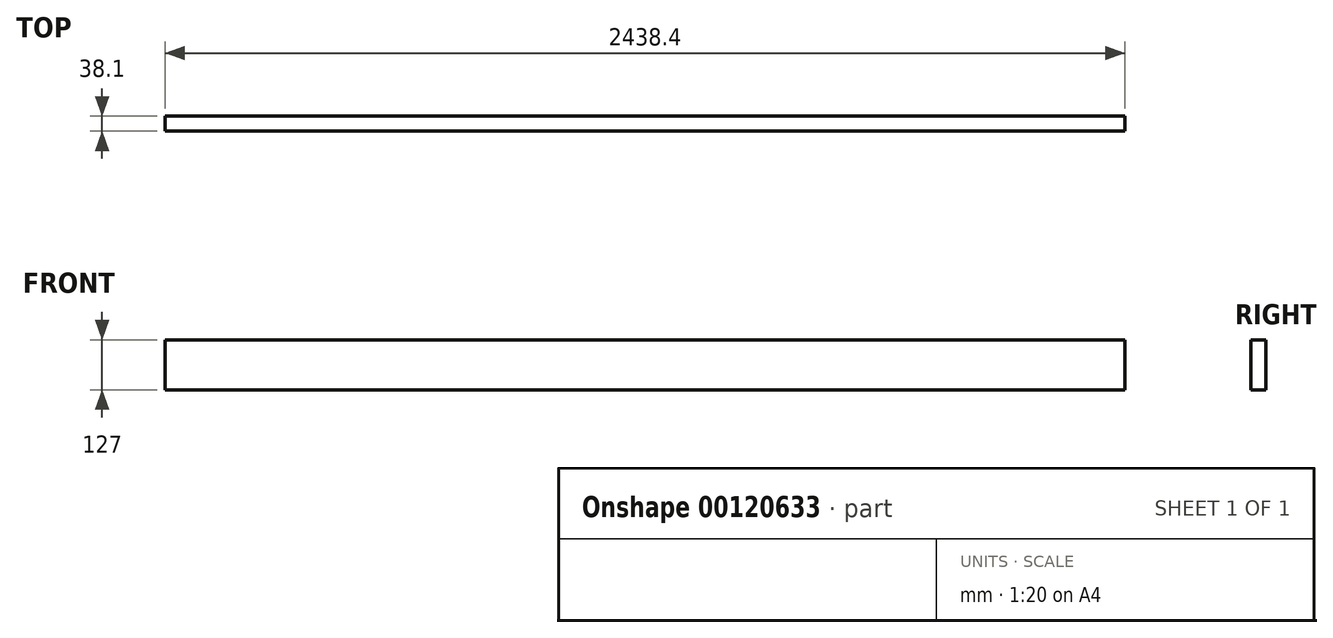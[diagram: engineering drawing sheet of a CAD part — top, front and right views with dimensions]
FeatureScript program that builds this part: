
annotation { "Feature Type Name" : "Feature", "Feature Type Description" : "" }
export const myFeature = defineFeature(function(context is Context, id is Id, definition is map)
    precondition{}
    {
        {
            var Q0;
            Q0=qCreatedBy(makeId("Top.planeOp"),FACE);
            var sketch = newSketch(context, id + "F0", { "sketchPlane" : qUnion([Q0])});
            skLineSegment(sketch, "E0.bottom", {"start": v(-1219.2, -19.05) * mm, "end": v(1219.2, -19.05) * mm});
            skLineSegment(sketch, "E0.top", {"start": v(-1219.2, 19.05) * mm, "end": v(1219.2, 19.05) * mm});
            skLineSegment(sketch, "E0.left", {"start": v(-1219.2, -19.05) * mm, "end": v(-1219.2, 19.05) * mm});
            skLineSegment(sketch, "E0.right", {"start": v(1219.2, -19.05) * mm, "end": v(1219.2, 19.05) * mm});
            skPoint(sketch, "E0.middle", {"position": v(0, 0) * mm});
            skSolve(sketch);
        }
        {
            var Q0;
            Q0 = qSketchRegion(id + "F0", true);
            extrude(context, id + "F1", {"entities" : qUnion([Q0]), "depth" : 127 * mm});
        }
    });
